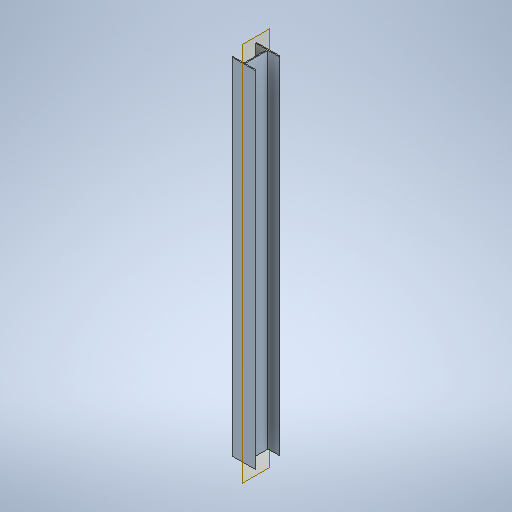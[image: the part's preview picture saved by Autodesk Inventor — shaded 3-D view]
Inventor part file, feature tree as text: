
AUTODESK INVENTOR PART (.ipt)
format: ipt  version: 2025.2 (Build 292293000, 293)  size: 267,776 bytes
history: native  units: in
note: dims shown in document units (in); Inventor stores cm internally (conversion verified against a paired STEP export)
features: other x3, plane x2, extrude x1
ambient origin geometry x8: Origin, YZ Plane, XZ Plane, XY Plane, X Axis, Y Axis, Z Axis, Center Point
bodies: Volumenkörper1 (feature_tree)
feature tree (6):
  other  "Skelett_Laufkatze.ipt"
  plane  "Arbeitsebene1"
  extrude  "Extrusion1"  Depth=0.3937in
  plane  "Arbeitsebene2"
  other  "I_Traeger_front"
  other  "I_Traeger_seite"
